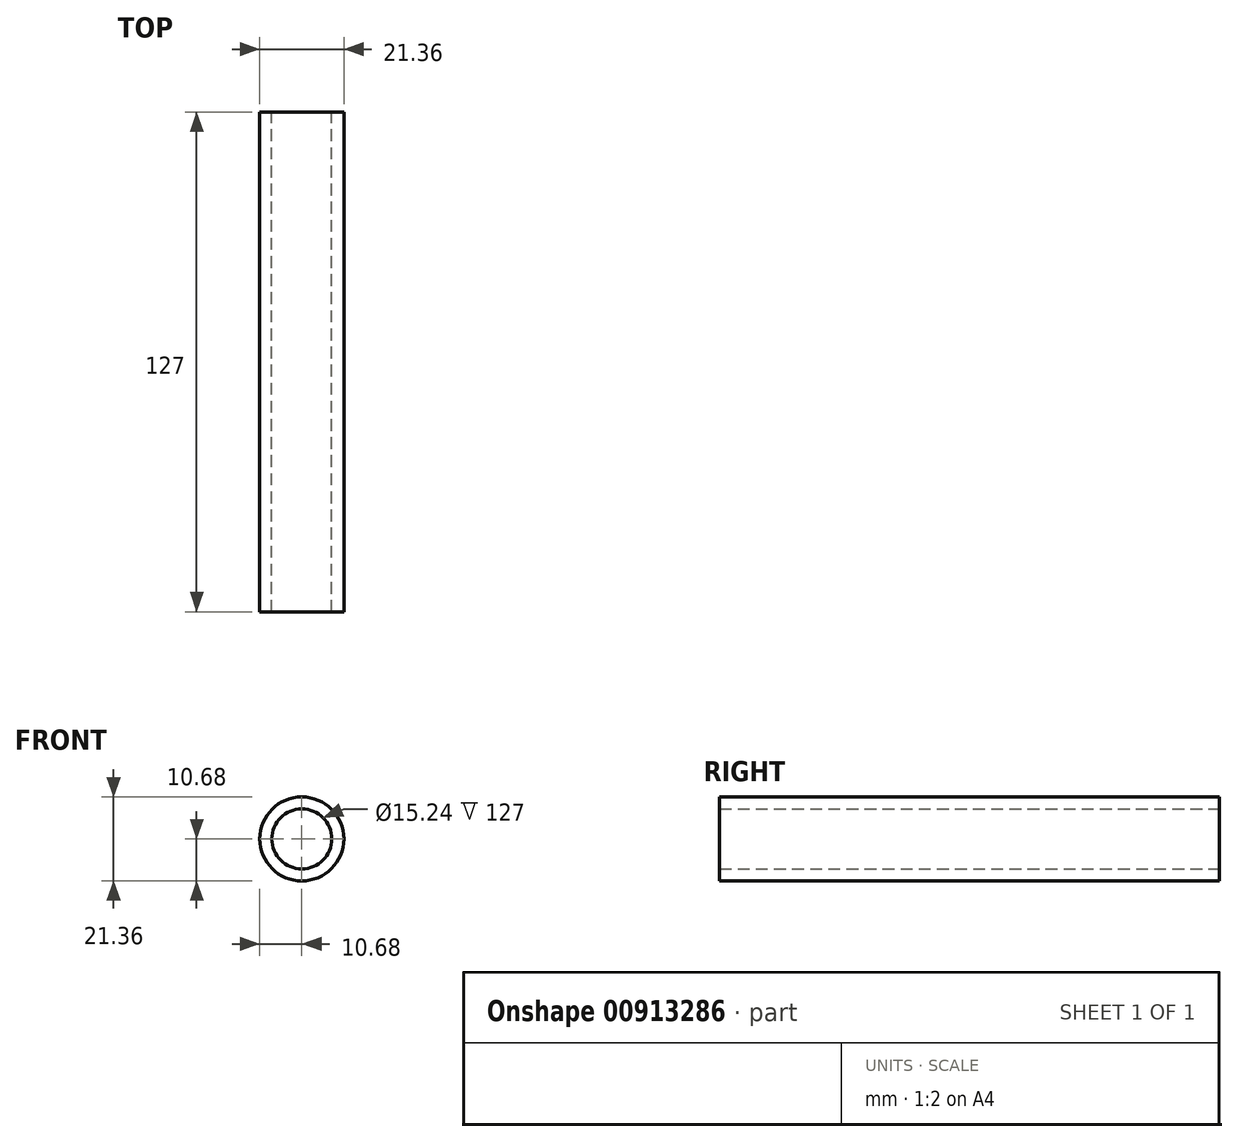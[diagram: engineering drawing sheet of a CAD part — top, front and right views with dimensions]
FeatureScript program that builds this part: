
annotation { "Feature Type Name" : "Feature", "Feature Type Description" : "" }
export const myFeature = defineFeature(function(context is Context, id is Id, definition is map)
    precondition{}
    {
        {
            var Q0;
            Q0=qCreatedBy(makeId("Front.planeOp"),FACE);
            var sketch = newSketch(context, id + "F0", { "sketchPlane" : qUnion([Q0])});
            skCircle(sketch, "E0", {"center": v(0, 0) * mm, "radius": 10.68 * mm});
            skCircle(sketch, "E1", {"center": v(0, 0) * mm, "radius": 7.62 * mm});
            skSolve(sketch);
        }
        {
            var Q0;
            Q0=makeQuery(id+"F0.imprint","IMPRINT",FACE,{"disambiguationData":[TD([[makeQuery(id+"F0.imprint","IMPRINT",EDGE,{"derivedFrom":sQuery(id+"F0.wireOp",EDGE,"E0")}),1.0]])]});
            extrude(context, id + "F1", {"entities" : qUnion([Q0]), "depth" : 127 * mm, "offsetDistance" : 25.4 * mm});
        }
    });
